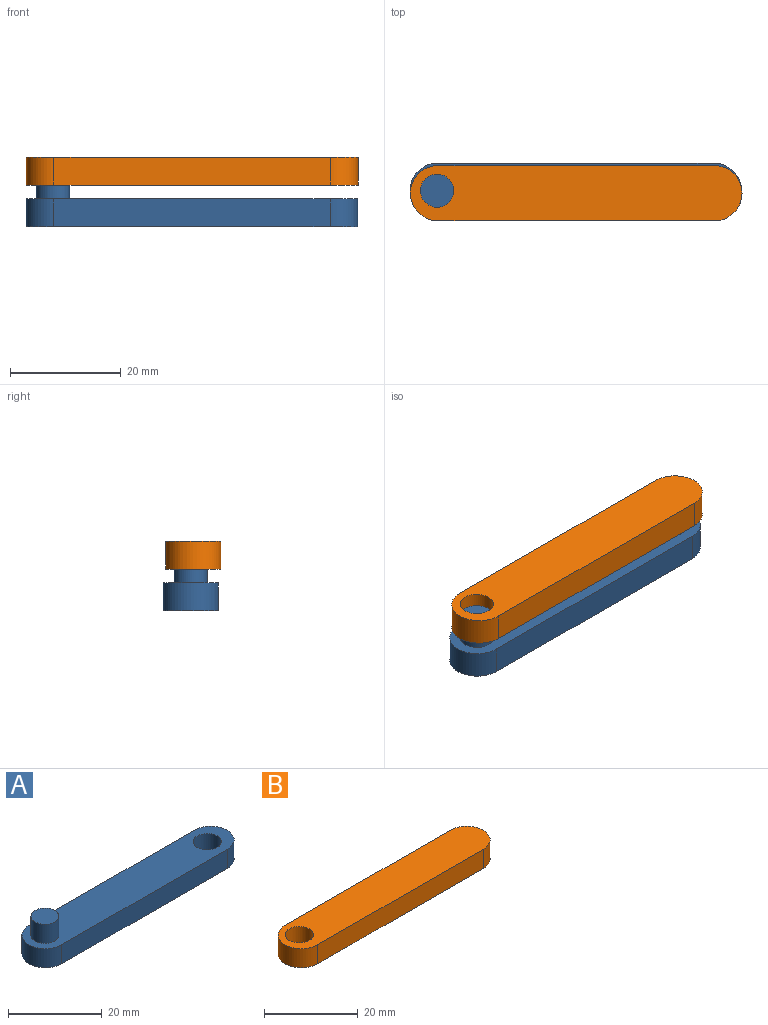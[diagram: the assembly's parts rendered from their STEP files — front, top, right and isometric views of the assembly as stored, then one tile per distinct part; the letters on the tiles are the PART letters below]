
ASSEMBLY  parts=2 mates=1
PART A: 9 faces, bbox 60x10x10 mm
  f0: plane 60x10mm, normal (0,0,1), area 522mm2, adj f1,f2,f3,f4,f6,f8
  f1: cylinder r=5mm len=10mm, axis (0,0,-1), area 78.5mm2, adj f0,f2,f4,f5
  f2: plane 50x5mm, normal (0,-1,0), area 250mm2, adj f0,f1,f3,f5
  f3: cylinder r=5mm len=10mm, axis (0,0,-1), area 78.5mm2, adj f0,f2,f4,f5
  f4: plane 50x5mm, normal (0,1,0), area 250mm2, adj f0,f1,f3,f5
  f5: plane 60x10mm, normal (0,0,-1), area 550.3mm2, adj f1,f2,f3,f4,f8
  f6: cylinder r=3mm len=6mm, axis (0,0,-1), area 94.2mm2, adj f0,f7
  f7: plane 6x6mm, normal (0,0,1), area 28.3mm2, adj f6
  f8: cylinder r=3mm len=6mm, axis (0,0,1), area 94.2mm2, adj f0,f5
PART B: 7 faces, bbox 60x10x5 mm
  f0: cylinder r=5mm len=10mm, axis (0,0,-1), area 78.5mm2, adj f1,f3,f4,f5
  f1: plane 50x5mm, normal (0,-1,0), area 250mm2, adj f0,f2,f4,f5
  f2: cylinder r=5mm len=10mm, axis (0,0,-1), area 78.5mm2, adj f1,f3,f4,f5
  f3: plane 50x5mm, normal (0,1,0), area 250mm2, adj f0,f2,f4,f5
  f4: plane 60x10mm, normal (0,0,1), area 550.3mm2, adj f0,f1,f2,f3,f6
  f5: plane 60x10mm, normal (0,0,-1), area 550.3mm2, adj f0,f1,f2,f3,f6
  f6: cylinder r=3mm len=6mm, axis (0,0,1), area 94.2mm2, adj f4,f5
PLACE A t=(2.1,10.26,2.85)mm
PLACE B t=(2.16,9.81,10.35)mm
MATE fastened A.f6 <-> B.f6  axis (0,0,1) through (-23.01,10.26,12.85)mm
